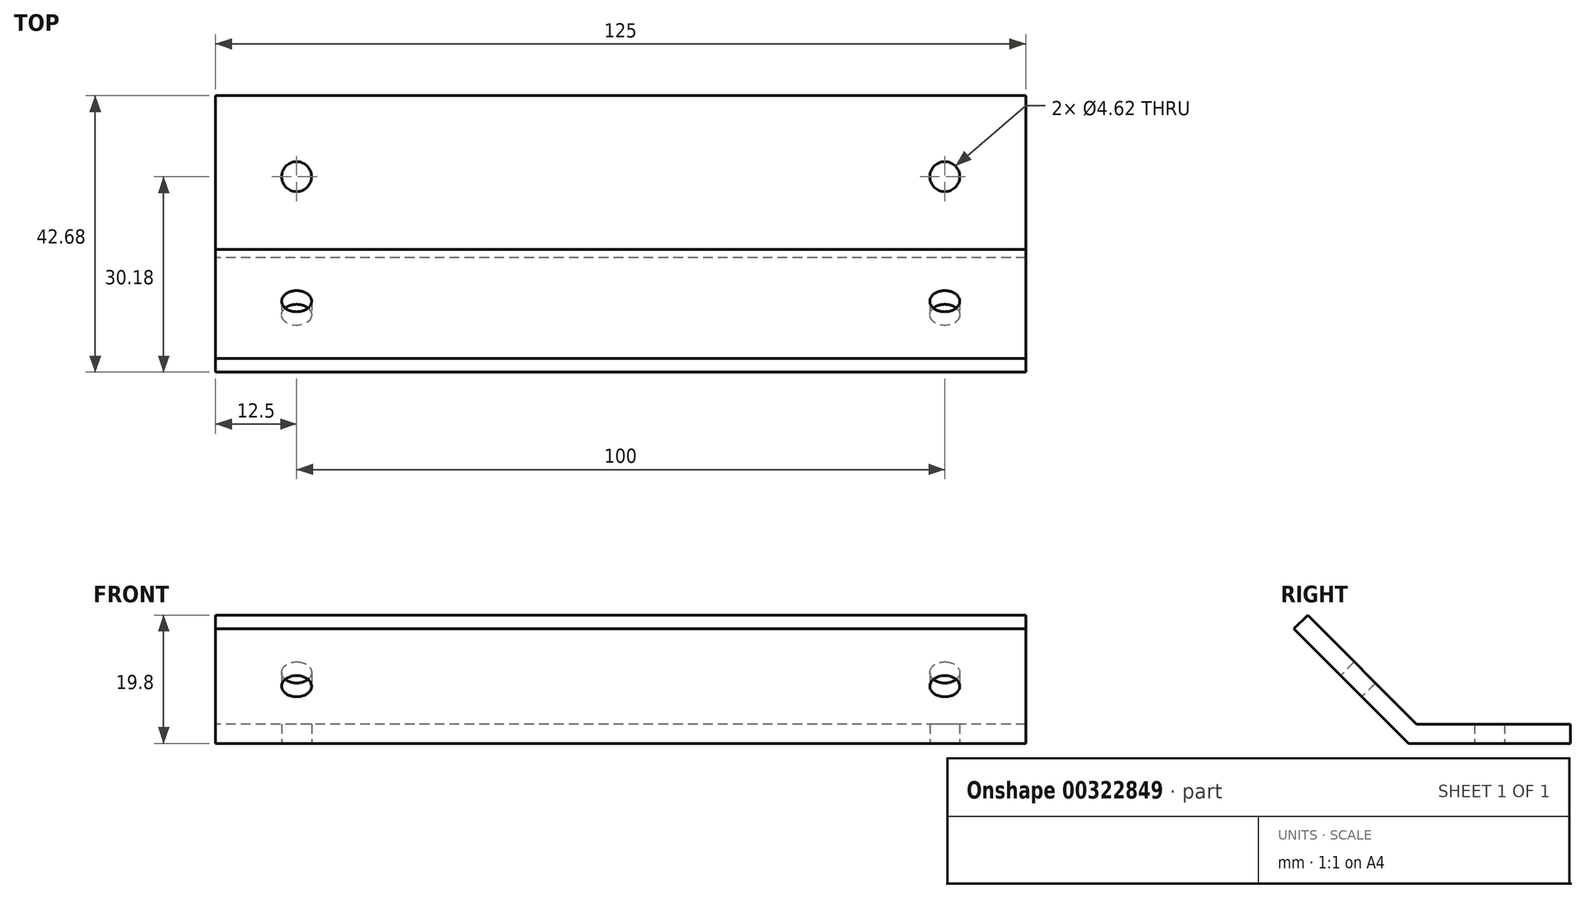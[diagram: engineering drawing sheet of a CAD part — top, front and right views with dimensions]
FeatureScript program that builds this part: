
annotation { "Feature Type Name" : "Feature", "Feature Type Description" : "" }
export const myFeature = defineFeature(function(context is Context, id is Id, definition is map)
    precondition{}
    {
        {
            var Q0;
            Q0=qCreatedBy(makeId("Right.planeOp"),FACE);
            var sketch = newSketch(context, id + "F0", { "sketchPlane" : qUnion([Q0])});
            skLineSegment(sketch, "E0.bottom", {"start": v(0, 0) * mm, "end": v(25, 0) * mm});
            skLineSegment(sketch, "E0.top", {"start": v(1.24, 3) * mm, "end": v(25, 3) * mm});
            skLineSegment(sketch, "E0.right", {"start": v(25, 0) * mm, "end": v(25, 3) * mm});
            skLineSegment(sketch, "E1", {"start": v(0, 0) * mm, "end": v(-17.68, 17.68) * mm});
            skLineSegment(sketch, "E2", {"start": v(-17.68, 17.68) * mm, "end": v(-15.56, 19.8) * mm});
            skLineSegment(sketch, "E3", {"start": v(-15.56, 19.8) * mm, "end": v(1.24, 3) * mm});
            skPoint(sketch, "E4.orphan", {"position": v(0, 3) * mm});
            skSolve(sketch);
        }
        {
            var Q0;
            Q0 = qSketchRegion(id + "F0", true);
            extrude(context, id + "F1", {"entities" : qUnion([Q0]), "depth" : 125 * mm});
        }
        {
            var Q0;
            Q0=makeQuery(id+"F1.opExtrude","SWEPT_FACE",FACE,{"disambiguationData":[OSD([sQuery(id+"F0.wireOp",EDGE,"E0.bottom")])]});
            var sketch = newSketch(context, id + "F2", { "sketchPlane" : qUnion([Q0])});
            skLineSegment(sketch, "E5", {"start": v(62.5, 0) * mm, "end": v(62.5, -12.5) * mm});
            skLineSegment(sketch, "E6", {"start": v(62.5, -12.5) * mm, "end": v(12.5, -12.5) * mm});
            skCircle(sketch, "E7", {"center": v(12.5, -12.5) * mm, "radius": 2.31 * mm});
            skCircle(sketch, "E8.MirrorC", {"center": v(112.5, -12.5) * mm, "radius": 2.31 * mm});
            skSolve(sketch);
        }
        {
            var Q0;
            Q0 = qSketchRegion(id + "F2", true);
            extrude(context, id + "F3", {"entities" : qUnion([Q0]), "operationType" : NewBodyOperationType.REMOVE, "oppositeDirection" : true, "depth" : 25 * mm});
        }
        {
            var Q0;
            Q0=makeQuery(id+"F1.opExtrude","SWEPT_FACE",FACE,{"disambiguationData":[OSD([sQuery(id+"F0.wireOp",EDGE,"E1")])]});
            var sketch = newSketch(context, id + "F4", { "sketchPlane" : qUnion([Q0])});
            skLineSegment(sketch, "E9", {"start": v(62.5, 0) * mm, "end": v(62.5, 12.5) * mm});
            skLineSegment(sketch, "E10", {"start": v(62.5, 12.5) * mm, "end": v(12.5, 12.5) * mm});
            skCircle(sketch, "E11", {"center": v(12.5, 12.5) * mm, "radius": 2.31 * mm});
            skCircle(sketch, "E12.MirrorC", {"center": v(112.5, 12.5) * mm, "radius": 2.31 * mm});
            skSolve(sketch);
        }
        {
            var Q0;
            Q0 = qSketchRegion(id + "F4", true);
            extrude(context, id + "F5", {"entities" : qUnion([Q0]), "operationType" : NewBodyOperationType.REMOVE, "oppositeDirection" : true, "depth" : 25 * mm});
        }
    });
